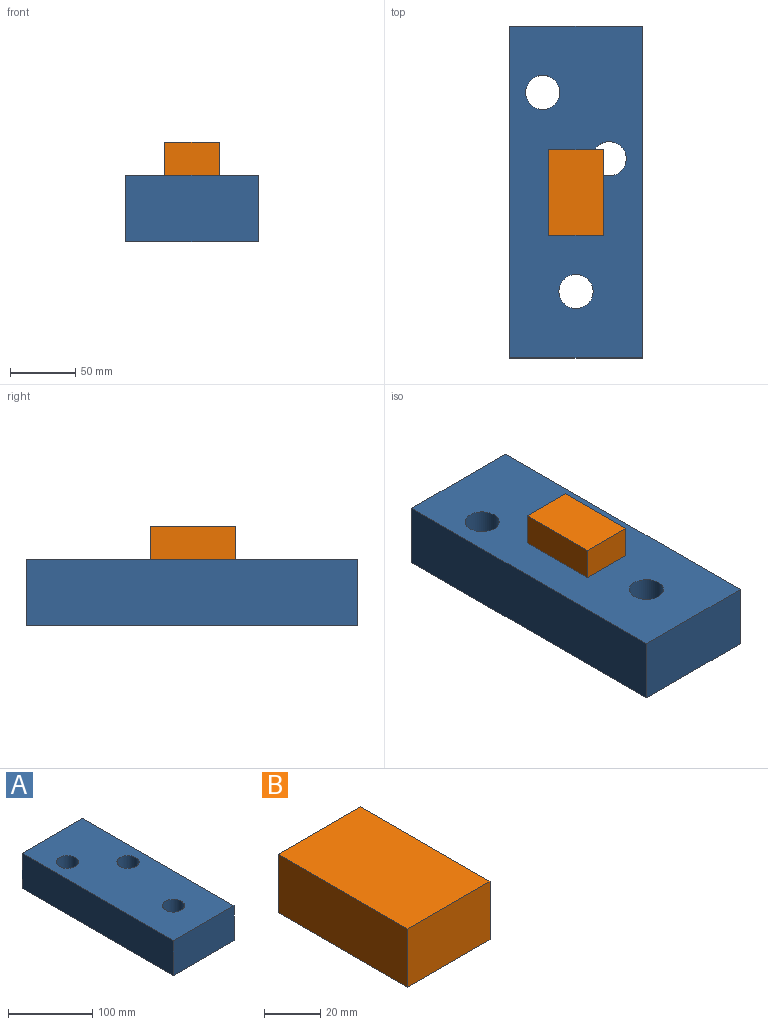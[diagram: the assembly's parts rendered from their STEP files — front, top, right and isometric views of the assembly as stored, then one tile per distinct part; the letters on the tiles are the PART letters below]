
ASSEMBLY  parts=2 mates=1
PART A: 9 faces, bbox 101.6x254x50.8 mm
  f0: plane 254x50.8mm, normal (1,0,0), area 12903.2mm2, adj f1,f3,f4,f5
  f1: plane 254x101.6mm, normal (0,0,1), area 24189.6mm2, adj f0,f2,f4,f5,f6,f7,f8
  f2: plane 254x50.8mm, normal (-1,0,0), area 12903.2mm2, adj f1,f3,f4,f5
  f3: plane 254x101.6mm, normal (0,0,-1), area 24189.6mm2, adj f0,f2,f4,f5,f6,f7,f8
  f4: plane 101.6x50.8mm, normal (0,-1,0), area 5161.3mm2, adj f0,f1,f2,f3
  f5: plane 101.6x50.8mm, normal (0,1,0), area 5161.3mm2, adj f0,f1,f2,f3
  f6: cylinder r=13.1mm len=50.8mm, axis (0,0,1), area 4180.5mm2, adj f1,f3
  f7: cylinder r=13.1mm len=50.8mm, axis (0,0,1), area 4180.5mm2, adj f1,f3
  f8: cylinder r=13.1mm len=50.8mm, axis (0,0,1), area 4180.5mm2, adj f1,f3
PART B: 6 faces, bbox 41.6x65.2x25.4 mm
  f0: plane 41.55x25.4mm, normal (0,1,0), area 1055.4mm2, adj f1,f3,f4,f5
  f1: plane 65.25x25.4mm, normal (-1,0,0), area 1657.3mm2, adj f0,f2,f4,f5
  f2: plane 41.55x25.4mm, normal (0,-1,0), area 1055.4mm2, adj f1,f3,f4,f5
  f3: plane 65.25x25.4mm, normal (1,0,0), area 1657.3mm2, adj f0,f2,f4,f5
  f4: plane 65.25x41.55mm, normal (0,0,1), area 2711mm2, adj f0,f1,f2,f3
  f5: plane 65.25x41.55mm, normal (0,0,-1), area 2711mm2, adj f0,f1,f2,f3
PLACE A t=(34.08,50.58,-166.68)mm
PLACE B t=(184.27,-73.56,-141.28)mm
MATE fastened A.f1 <-> B.f5  axis (0,0,1) through (34.08,-76.99,-141.28)mm
